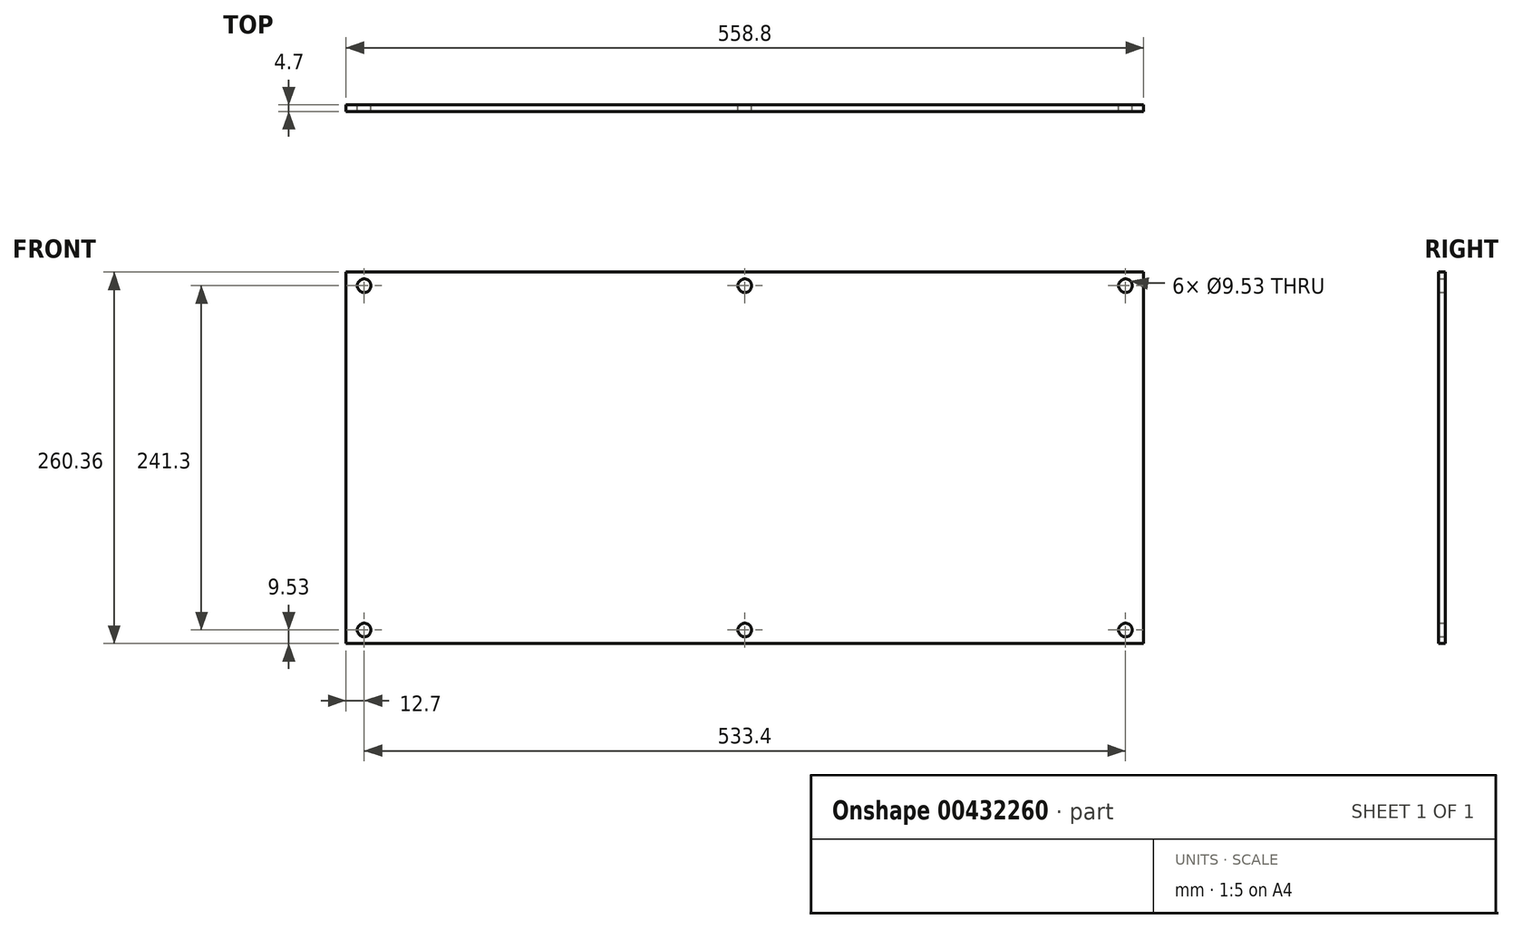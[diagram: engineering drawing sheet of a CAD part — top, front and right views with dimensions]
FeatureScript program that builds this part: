
annotation { "Feature Type Name" : "Feature", "Feature Type Description" : "" }
export const myFeature = defineFeature(function(context is Context, id is Id, definition is map)
    precondition{}
    {
        {
            var Q0;
            Q0=qCreatedBy(makeId("Front.planeOp"),FACE);
            var sketch = newSketch(context, id + "F0", { "sketchPlane" : qUnion([Q0])});
            skLineSegment(sketch, "E0.bottom", {"start": v(279.4, 130.18) * mm, "end": v(-279.4, 130.18) * mm});
            skLineSegment(sketch, "E0.top", {"start": v(279.4, -130.18) * mm, "end": v(-279.4, -130.18) * mm});
            skLineSegment(sketch, "E0.left", {"start": v(279.4, 130.18) * mm, "end": v(279.4, -130.18) * mm});
            skLineSegment(sketch, "E0.right", {"start": v(-279.4, 130.18) * mm, "end": v(-279.4, -130.18) * mm});
            skPoint(sketch, "E0.middle", {"position": v(0, 0) * mm});
            skLineSegment(sketch, "E1", {"start": v(-325.36, 0) * mm, "end": v(307.54, 0) * mm, "construction": true});
            skPoint(sketch, "E1.startSnap0", {"position": v(-279.4, 0) * mm});
            skLineSegment(sketch, "E2", {"start": v(0, 155.68) * mm, "end": v(0, -161.93) * mm, "construction": true});
            skPoint(sketch, "E2.startSnap0", {"position": v(0, 130.18) * mm});
            skPoint(sketch, "E2.endSnap0", {"position": v(0, -130.18) * mm});
            skCircle(sketch, "E3", {"center": v(-266.7, 120.65) * mm, "radius": 4.76 * mm});
            skCircle(sketch, "E4", {"center": v(0, 120.65) * mm, "radius": 4.76 * mm});
            skCircle(sketch, "E5", {"center": v(266.7, 120.65) * mm, "radius": 4.76 * mm});
            skCircle(sketch, "E6", {"center": v(266.7, -120.65) * mm, "radius": 4.76 * mm});
            skCircle(sketch, "E7", {"center": v(0, -120.65) * mm, "radius": 4.76 * mm});
            skCircle(sketch, "E8", {"center": v(-266.7, -120.65) * mm, "radius": 4.76 * mm});
            skSolve(sketch);
        }
        {
            var Q0;
            Q0 = qSketchRegion(id + "F0", true);
            extrude(context, id + "F1", {"entities" : qUnion([Q0]), "depth" : 4.7 * mm, "offsetDistance" : 25.4 * mm});
        }
    });
